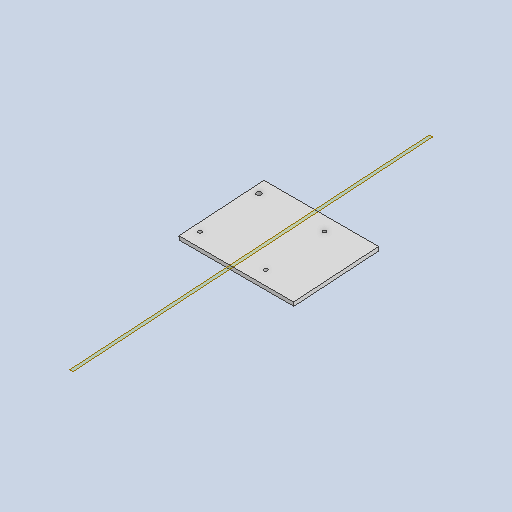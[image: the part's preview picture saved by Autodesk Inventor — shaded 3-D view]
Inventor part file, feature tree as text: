
AUTODESK INVENTOR PART (.ipt)
format: ipt  version: 2023.2 (Build 272271000, 271)  size: 102,912 bytes
history: native  units: mm
features: other x3, plane x1, extrude x1, sketch x1
ambient origin geometry x8: Origin, YZ Plane, XZ Plane, XY Plane, X Axis, Y Axis, Z Axis, Center Point
bodies: Body1 (feature_tree)
feature tree (6):
  plane  "Work Plane1"
  extrude  "Extrusion2"  Depth=6.0mm TaperAngle=0.0deg
  sketch  "Sketch2"  dims[d15=125.0mm d16=130.0mm d17=12.3mm d18=12.3mm d19=5.1mm d20=5.1mm d21=5.1mm d22=7.1mm d23=50.0mm d24=20.0mm d25=20.0mm d26=20.0mm d27=20.0mm d28=6.0mm d29=0.0mm]
  parser-record x1  (decoder bookkeeping rows leaked as tree rows — omitted from the tree; the rows remain in map.json)
  other  "Main Assembly.iam"
  other  "C beam extrusion 500:1"
note: 1 file-system path scrubbed to <path> (originals preserved in map.json)
